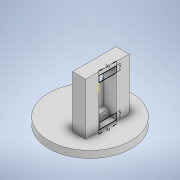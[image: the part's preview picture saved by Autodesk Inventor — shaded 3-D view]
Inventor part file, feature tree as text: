
AUTODESK INVENTOR PART (.ipt)
format: ipt  version: 2022 (Build 260153000, 153)  size: 338,944 bytes
history: native  units: in
note: dims shown in document units (in); Inventor stores cm internally (conversion verified against a paired STEP export)
features: sketch x21, extrude x16
ambient origin geometry x8: Origin, YZ Plane, XZ Plane, XY Plane, X Axis, Y Axis, Z Axis, Center Point
bodies: Solid1 (feature_tree)
feature tree (37):
  extrude  "Extrusion1"  Depth=0.2362in TaperAngle=0.0deg
  extrude  "Extrusion2"  Depth=0.1181in
  extrude  "Extrusion3"  Depth=0.2362in TaperAngle=0.0deg
  extrude  "Extrusion4"  Depth=0.3937in
  extrude  "Extrusion5"  Depth=0.5906in
  extrude  "Extrusion6"  Depth=0.9843in
  extrude  "Extrusion7"  Depth=0.0787in
  sketch  "Sketch8"  dims[d17=1.5748in d18=0.7874in]
  extrude  "Extrusion8"  Depth=0.7874in
  extrude  "Extrusion9"  Depth=0.1969in
  sketch  "Sketch11"  dims[d24=1.4173in d25=0.1063in]
  extrude  "Extrusion10"  Depth=0.1969in
  extrude  "Extrusion11"  Depth=0.1063in
  extrude  "Extrusion12"  Depth=0.7874in TaperAngle=0.0deg
  extrude  "Extrusion13"  Depth=0.5512in
  sketch  "Sketch17"  dims[d35=0.7874in d36=0.0in d37=0.3937in]
  sketch  "Sketch18"  dims[d38=1.9685in]
  sketch  "Sketch19"  dims[d39=0.1969in]
  extrude  "Extrusion14"  Depth=0.5512in
  extrude  "Extrusion15"  Depth=0.1063in
  extrude  "Extrusion16"  Depth=0.3937in
  sketch  "Sketch1"  dims[d0=3.7402in d1=0.2362in d2=0.0in]
  sketch  "Sketch2"  dims[d3=0.5512in d4=0.1181in]
  sketch  "Sketch3"  dims[d5=0.1181in d6=0.2362in d7=0.0in]
  sketch  "Sketch4"  dims[d8=0.1969in d9=0.3937in]
  sketch  "Sketch5"  dims[d10=0.3937in d11=0.5906in]
  sketch  "Sketch6"  dims[d12=0.9843in d13=0.9843in]
  sketch  "Sketch7"  dims[d14=2.3622in d15=0.0in d16=0.0787in]
  sketch  "Sketch9"  dims[d19=0.7874in d20=0.0in d21=0.1969in]
  sketch  "Sketch10"  dims[d22=1.4173in d23=0.1969in]
  sketch  "Sketch12"  dims[d26=0.1063in d27=0.7874in d28=0.0in]
  sketch  "Sketch13"  dims[d29=0.1969in d30=0.5512in]
  sketch  "Sketch14"  dims[d31=0.1969in d32=0.5512in]
  sketch  "Sketch16"  dims[d33=0.1063in d34=0.1063in]
  sketch  "Sketch20"  dims[d40=0.3937in]
  sketch  "Sketch21"  dims[d41=0.3937in]
  sketch  "Sketch22"  dims[d42=0.3937in d43=1.2205in d44=1.5748in d45=0.5512in d46=0.0in d47=0.7874in d48=0.2756in d49=0.7874in d50=0.2756in d51=0.2756in d52=0.4724in d53=0.0in d54=0.0787in d55=0.0in d56=0.1181in d57=0.5438in d58=0.0in d59=0.1181in d60=0.0787in d61=0.0in d62=0.5512in d63=0.7874in d64=1.5748in d65=0.7874in d66=1.5748in d67=0.1575in d68=0.1575in d69=0.1575in d70=0.1575in d71=0.1181in d72=0.0in d73=0.1181in d74=0.0in d75=0.315in d76=0.0in d77=0.0787in d78=0.0in d79=0.1575in d80=0.0in]
